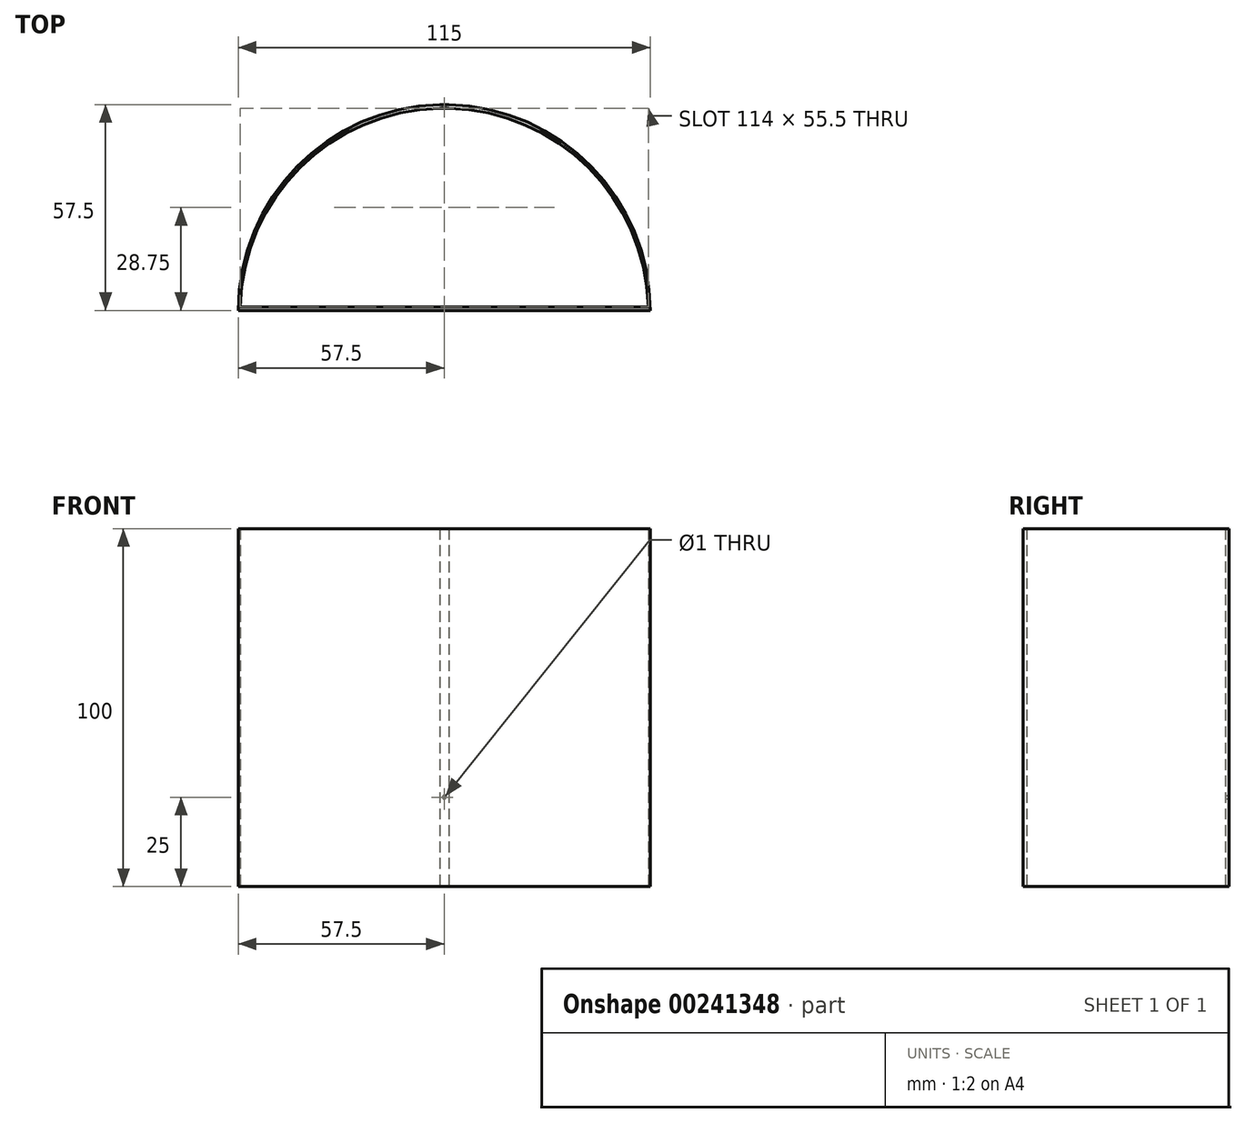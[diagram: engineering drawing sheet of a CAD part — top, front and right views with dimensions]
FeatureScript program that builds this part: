
annotation { "Feature Type Name" : "Feature", "Feature Type Description" : "" }
export const myFeature = defineFeature(function(context is Context, id is Id, definition is map)
    precondition{}
    {
        {
            var Q0;
            Q0=qCreatedBy(makeId("Top.planeOp"),FACE);
            var sketch = newSketch(context, id + "F0", { "sketchPlane" : qUnion([Q0])});
            skLineSegment(sketch, "E0", {"start": v(-57.5, 0) * mm, "end": v(57.5, 0) * mm});
            skLineSegment(sketch, "E1", {"start": v(-1.25, 57.5) * mm, "end": v(1.25, 57.5) * mm});
            skArc(sketch, "E2", {"start": v(-1.25, 57.5) * mm, "mid": v(-41.1, 40.22) * mm, "end": v(-57.5, 0) * mm});
            skArc(sketch, "E3", {"start": v(57.5, 0) * mm, "mid": v(41.1, 40.22) * mm, "end": v(1.25, 57.5) * mm});
            skLineSegment(sketch, "E4", {"start": v(-1.25, 56.5) * mm, "end": v(1.25, 56.5) * mm});
            skLineSegment(sketch, "E5", {"start": v(-57, 1) * mm, "end": v(57, 1) * mm});
            skArc(sketch, "E6", {"start": v(-1.25, 56.5) * mm, "mid": v(-40.23, 39.9) * mm, "end": v(-57, 1) * mm});
            skArc(sketch, "E7", {"start": v(57, 1) * mm, "mid": v(40.23, 39.9) * mm, "end": v(1.25, 56.5) * mm});
            skSolve(sketch);
        }
        {
            var Q0;
            Q0 = qSketchRegion(id + "F0", true);
            var Q1;
            Q1=sQuery(id+"F0.wireOp",EDGE,"E0");
            var Q2;
            Q2=sQuery(id+"F0.wireOp",EDGE,"E2");
            var Q3;
            Q3=sQuery(id+"F0.wireOp",EDGE,"E1");
            var Q4;
            Q4=sQuery(id+"F0.wireOp",EDGE,"E3");
            extrude(context, id + "F1", {"entities" : qUnion([Q0]), "surfaceEntities" : qUnion([Q1, Q2, Q3, Q4]), "depth" : 100 * mm, "offsetDistance" : 25 * mm});
        }
        {
            var Q0;
            Q0=makeQuery(id+"F1.opExtrude","SWEPT_FACE",FACE,{"disambiguationData":[OSD([sQuery(id+"F0.wireOp",EDGE,"E1")])]});
            var sketch = newSketch(context, id + "F2", { "sketchPlane" : qUnion([Q0])});
            skCircle(sketch, "E8", {"center": v(0, 25) * mm, "radius": 0.5 * mm});
            skPoint(sketch, "E8.centerSnap0", {"position": v(1.25, 50) * mm});
            skSolve(sketch);
        }
        {
            var Q0;
            Q0 = qSketchRegion(id + "F2", true);
            extrude(context, id + "F3", {"entities" : qUnion([Q0]), "operationType" : NewBodyOperationType.REMOVE, "oppositeDirection" : true, "depth" : 25 * mm, "offsetDistance" : 25 * mm});
        }
    });
